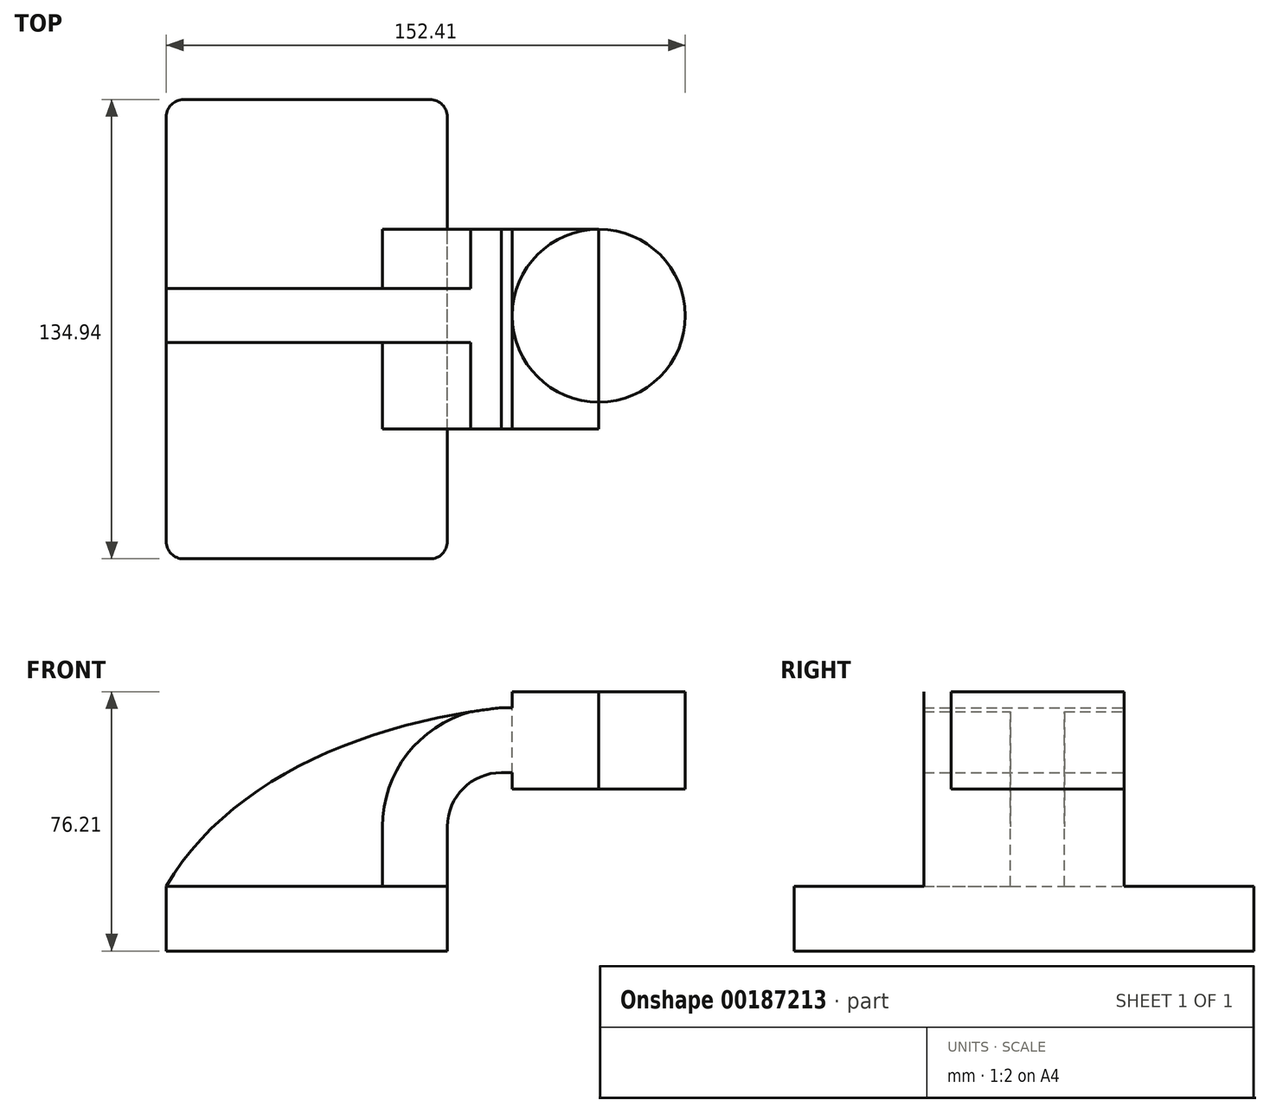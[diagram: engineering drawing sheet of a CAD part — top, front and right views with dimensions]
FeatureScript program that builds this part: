
annotation { "Feature Type Name" : "Feature", "Feature Type Description" : "" }
export const myFeature = defineFeature(function(context is Context, id is Id, definition is map)
    precondition{}
    {
        {
            var Q0;
            Q0=qCreatedBy(makeId("Front.planeOp"),FACE);
            var sketch = newSketch(context, id + "F0", { "sketchPlane" : qUnion([Q0])});
            skLineSegment(sketch, "E0.bottom", {"start": v(-41.28, 9.52) * mm, "end": v(41.27, 9.53) * mm});
            skLineSegment(sketch, "E0.top", {"start": v(-41.28, -9.53) * mm, "end": v(41.28, -9.53) * mm});
            skLineSegment(sketch, "E0.left", {"start": v(-41.28, 9.52) * mm, "end": v(-41.28, -9.53) * mm});
            skLineSegment(sketch, "E0.right", {"start": v(41.27, 9.53) * mm, "end": v(41.28, -9.52) * mm});
            skPoint(sketch, "E0.middle", {"position": v(0, 0) * mm});
            skLineSegment(sketch, "E1.bottom", {"start": v(60.33, 38.1) * mm, "end": v(111.13, 38.1) * mm});
            skLineSegment(sketch, "E1.top", {"start": v(60.33, 66.68) * mm, "end": v(111.13, 66.68) * mm});
            skLineSegment(sketch, "E1.left", {"start": v(60.33, 38.1) * mm, "end": v(60.33, 66.67) * mm});
            skLineSegment(sketch, "E1.right", {"start": v(111.13, 38.1) * mm, "end": v(111.13, 66.67) * mm});
            skPoint(sketch, "E1.middle", {"position": v(85.73, 52.39) * mm});
            skLineSegment(sketch, "E2", {"start": v(41.27, 9.53) * mm, "end": v(41.27, 27) * mm});
            skArc(sketch, "E3", {"start": v(41.27, 27) * mm, "mid": v(45.92, 38.23) * mm, "end": v(57.15, 42.88) * mm});
            skLineSegment(sketch, "E4", {"start": v(57.15, 42.88) * mm, "end": v(85.73, 42.88) * mm});
            skLineSegment(sketch, "E5.0", {"start": v(57.15, 61.93) * mm, "end": v(85.73, 61.93) * mm});
            skArc(sketch, "E5.1", {"start": v(22.22, 27) * mm, "mid": v(32.45, 51.7) * mm, "end": v(57.15, 61.93) * mm});
            skLineSegment(sketch, "E5.2", {"start": v(22.22, 9.53) * mm, "end": v(22.22, 27) * mm});
            skLineSegment(sketch, "E6", {"start": v(85.73, 38.1) * mm, "end": v(85.73, 66.68) * mm});
            skFitSpline(sketch, "E7", {"points": [v(-41.28, 9.53) * mm, v(57.15, 61.93) * mm], "startDerivative": vector(53.2, 92.15) * mm, "endDerivative": vector(122.2, 13.1) * mm});
            skSolve(sketch);
        }
        {
            var Q0;
            Q0=makeQuery(id+"F0.imprint","IMPRINT",FACE,{"disambiguationData":[TD([[makeQuery(id+"F0.imprint","IMPRINT",EDGE,{"derivedFrom":sQuery(id+"F0.wireOp",EDGE,"E0.top")}),1.0]])]});
            extrude(context, id + "F1", {"entities" : qUnion([Q0]), "endBound" : BoundingType.SYMMETRIC, "depth" : 127 * mm});
        }
        {
            var Q0;
            {var subQ1=sQuery(id+"F0.wireOp",EDGE,"E2");Q0=makeQuery(id+"F0.imprint","IMPRINT",FACE,{"disambiguationData":[TD([[makeQuery(id+"F0.imprint","IMPRINT",EDGE,{"derivedFrom":subQ1}),1.0]])]});}
            var Q1;
            {var subQ0=sQuery(id+"F0.wireOp",EDGE,"E1.left");var subQ1=sQuery(id+"F0.wireOp",EDGE,"E1.bottom");var subQ2=makeQuery(id+"F0.imprint","INTERSECT",VERTEX,{"derivedFrom":[subQ1,subQ0]});Q1=makeQuery(id+"F0.imprint","IMPRINT",FACE,{"disambiguationData":[TD([[makeQuery(id+"F0.imprint","IMPRINT",EDGE,{"disambiguationData":[TD([[subQ2,-1.0]])],"derivedFrom":subQ1}),1.0]])]});}
            var Q2;
            {var subQ0=sQuery(id+"F0.wireOp",EDGE,"E4");var subQ1=sQuery(id+"F0.wireOp",EDGE,"E1.left");var subQ2=makeQuery(id+"F0.imprint","INTERSECT",VERTEX,{"derivedFrom":[subQ1,subQ0]});Q2=makeQuery(id+"F0.imprint","IMPRINT",FACE,{"disambiguationData":[TD([[makeQuery(id+"F0.imprint","IMPRINT",EDGE,{"disambiguationData":[TD([[subQ2,-1.0]])],"derivedFrom":subQ1}),-1.0]])]});}
            var Q3;
            {var subQ0=sQuery(id+"F0.wireOp",EDGE,"E1.left");var subQ1=sQuery(id+"F0.wireOp",EDGE,"E1.top");var subQ2=makeQuery(id+"F0.imprint","INTERSECT",VERTEX,{"derivedFrom":[subQ1,subQ0]});Q3=makeQuery(id+"F0.imprint","IMPRINT",FACE,{"disambiguationData":[TD([[makeQuery(id+"F0.imprint","IMPRINT",EDGE,{"disambiguationData":[TD([[subQ2,-1.0]])],"derivedFrom":subQ1}),-1.0]])]});}
            extrude(context, id + "F2", {"entities" : qUnion([Q0, Q1, Q2, Q3]), "endBound" : BoundingType.SYMMETRIC, "depth" : 50.8 * mm});
        }
        {
            var Q0;
            Q0=makeQuery(id+"F1.opExtrude","CAP_FACE",FACE,{"disambiguationData":[OSD([sQuery(id+"F0.wireOp",EDGE,"E0.bottom"),sQuery(id+"F0.wireOp",EDGE,"E0.top"),sQuery(id+"F0.wireOp",EDGE,"E0.left"),sQuery(id+"F0.wireOp",EDGE,"E0.right")])],"isStart":false});
            var Q1;
            Q1=makeQuery(id+"F2.opExtrude","CAP_FACE",FACE,{"disambiguationData":[OSD([sQuery(id+"F0.wireOp",EDGE,"E0.bottom"),sQuery(id+"F0.wireOp",EDGE,"E1.bottom"),sQuery(id+"F0.wireOp",EDGE,"E1.top"),sQuery(id+"F0.wireOp",EDGE,"E1.left"),sQuery(id+"F0.wireOp",EDGE,"E2"),sQuery(id+"F0.wireOp",EDGE,"E3"),sQuery(id+"F0.wireOp",EDGE,"E4"),sQuery(id+"F0.wireOp",EDGE,"E5.0"),sQuery(id+"F0.wireOp",EDGE,"E5.1"),sQuery(id+"F0.wireOp",EDGE,"E5.2"),sQuery(id+"F0.wireOp",EDGE,"E6"),sQuery(id+"F0.wireOp",EDGE,"E7")])],"isStart":false});
            var Q2;
            {var subQ3=sQuery(id+"F0.wireOp",EDGE,"E5.2");Q2=makeQuery(id+"F0.imprint","IMPRINT",FACE,{"disambiguationData":[TD([[makeQuery(id+"F0.imprint","IMPRINT",EDGE,{"derivedFrom":subQ3}),1.0]])]});}
            extrude(context, id + "F3", {"entities" : qUnion([Q0, Q1, Q2]), "operationType" : NewBodyOperationType.ADD, "endBound" : BoundingType.SYMMETRIC, "depth" : 15.88 * mm});
        }
        {
            var Q0;
            {var subQ0=sQuery(id+"F0.wireOp",EDGE,"E1.right");Q0=makeQuery(id+"F0.imprint","IMPRINT",FACE,{"disambiguationData":[TD([[makeQuery(id+"F0.imprint","IMPRINT",EDGE,{"derivedFrom":subQ0}),1.0]])]});}
            var Q1;
            Q1=sQuery(id+"F0.wireOp",EDGE,"E6");
            revolve(context, id + "F4", {"entities" : qUnion([Q0]), "axis" : qUnion([Q1]), "revolveType" : RevolveType.FULL, "oppositeDirection" : true});
        }
        {
            var Q0;
            Q0=makeQuery(id+"F3.opExtrude","CAP_EDGE",EDGE,{"disambiguationData":[OSD([sQuery(id+"F0.wireOp",EDGE,"E0.left")])],"isStart":false});
            var Q1;
            Q1=makeQuery(id+"F3.opExtrude","CAP_EDGE",EDGE,{"disambiguationData":[OSD([sQuery(id+"F0.wireOp",EDGE,"E0.right")])],"isStart":false});
            var Q2;
            Q2=makeQuery(id+"F1.opExtrude","CAP_EDGE",EDGE,{"disambiguationData":[OSD([sQuery(id+"F0.wireOp",EDGE,"E0.right")])],"isStart":true});
            var Q3;
            Q3=makeQuery(id+"F1.opExtrude","CAP_EDGE",EDGE,{"disambiguationData":[OSD([sQuery(id+"F0.wireOp",EDGE,"E0.left")])],"isStart":true});
            fillet(context, id + "F5", {"entities" : qUnion([Q0, Q1, Q2, Q3]), "radius" : 5.08 * mm, "tangentPropagation" : true, "allowEdgeOverflow" : false});
        }
    });
